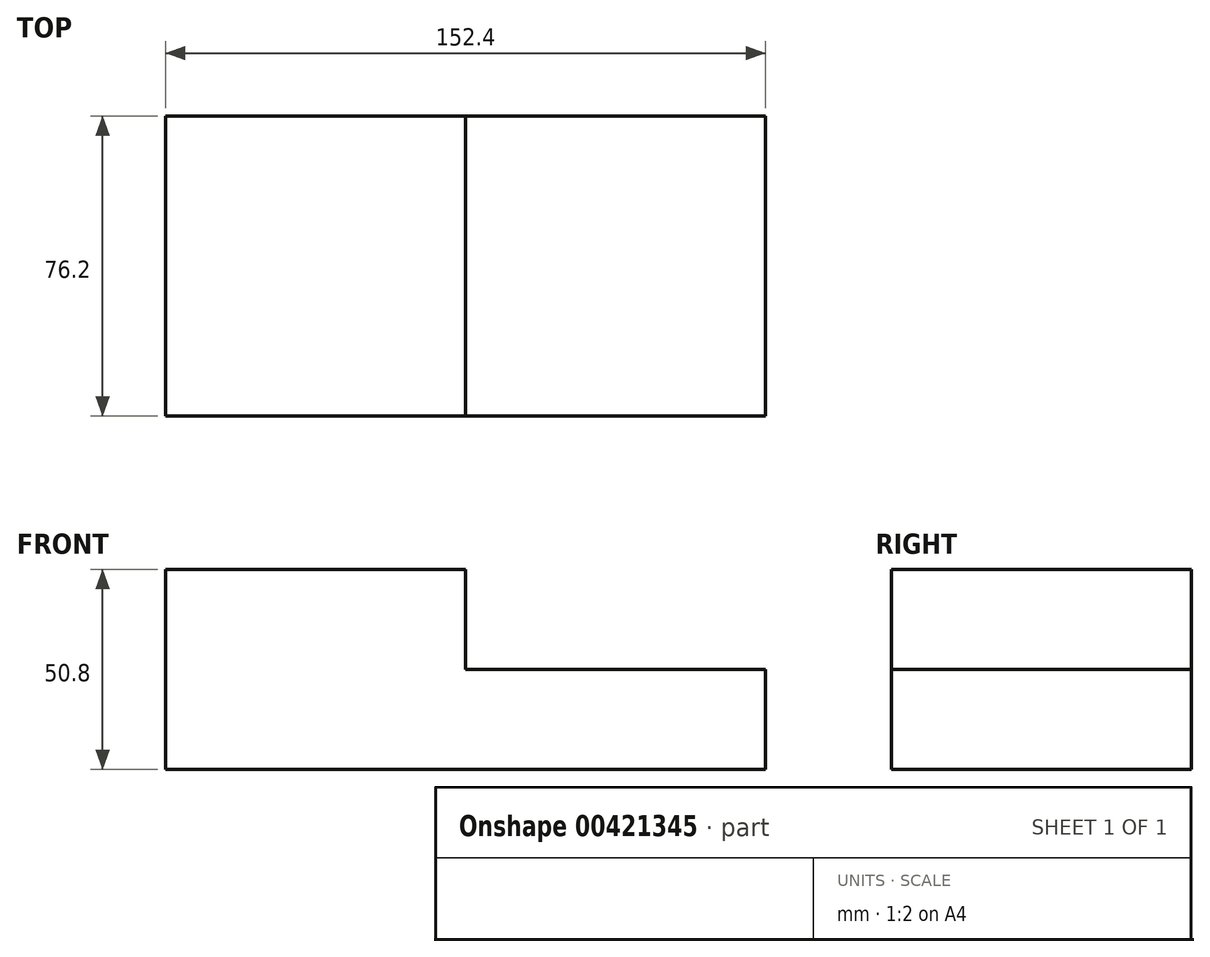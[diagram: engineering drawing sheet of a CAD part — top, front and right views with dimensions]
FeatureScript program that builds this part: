
annotation { "Feature Type Name" : "Feature", "Feature Type Description" : "" }
export const myFeature = defineFeature(function(context is Context, id is Id, definition is map)
    precondition{}
    {
        {
            var Q0;
            Q0=qCreatedBy(makeId("Front.planeOp"),FACE);
            var sketch = newSketch(context, id + "F0", { "sketchPlane" : qUnion([Q0])});
            skLineSegment(sketch, "E0", {"start": v(0, 0) * mm, "end": v(152.4, 0) * mm});
            skLineSegment(sketch, "E1", {"start": v(0, 0) * mm, "end": v(0, 50.8) * mm});
            skLineSegment(sketch, "E2", {"start": v(0, 50.8) * mm, "end": v(76.2, 50.8) * mm});
            skLineSegment(sketch, "E3", {"start": v(76.2, 50.8) * mm, "end": v(76.2, 25.4) * mm});
            skLineSegment(sketch, "E4", {"start": v(76.2, 25.4) * mm, "end": v(152.4, 25.4) * mm});
            skLineSegment(sketch, "E5", {"start": v(152.4, 25.4) * mm, "end": v(152.4, 0) * mm});
            skSolve(sketch);
        }
        {
            var Q0;
            Q0 = qSketchRegion(id + "F0", true);
            extrude(context, id + "F1", {"entities" : qUnion([Q0]), "depth" : 76.2 * mm});
        }
    });
